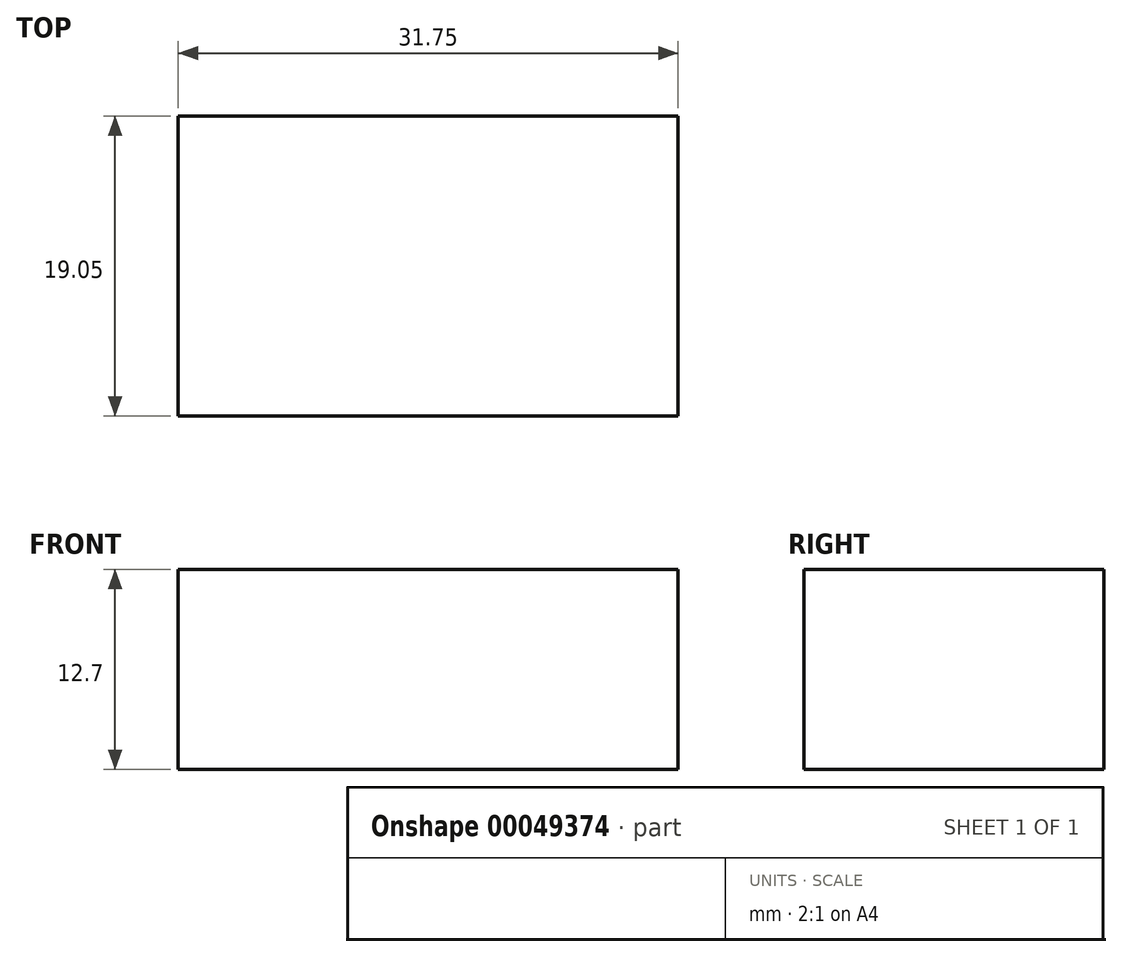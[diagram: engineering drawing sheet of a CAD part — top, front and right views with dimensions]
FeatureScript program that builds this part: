
annotation { "Feature Type Name" : "Feature", "Feature Type Description" : "" }
export const myFeature = defineFeature(function(context is Context, id is Id, definition is map)
    precondition{}
    {
        {
            var Q0;
            Q0=qCreatedBy(makeId("Top.planeOp"),FACE);
            var sketch = newSketch(context, id + "F0", { "sketchPlane" : qUnion([Q0])});
            skLineSegment(sketch, "E0.bottom", {"start": v(0, 0) * mm, "end": v(31.75, 0) * mm});
            skLineSegment(sketch, "E0.top", {"start": v(0, -19.05) * mm, "end": v(31.75, -19.05) * mm});
            skLineSegment(sketch, "E0.left", {"start": v(0, 0) * mm, "end": v(0, -19.05) * mm});
            skLineSegment(sketch, "E0.right", {"start": v(31.75, 0) * mm, "end": v(31.75, -19.05) * mm});
            skSolve(sketch);
        }
        {
            var Q0;
            Q0 = qSketchRegion(id + "F0", true);
            extrude(context, id + "F1", {"entities" : qUnion([Q0]), "depth" : 12.7 * mm});
        }
    });
